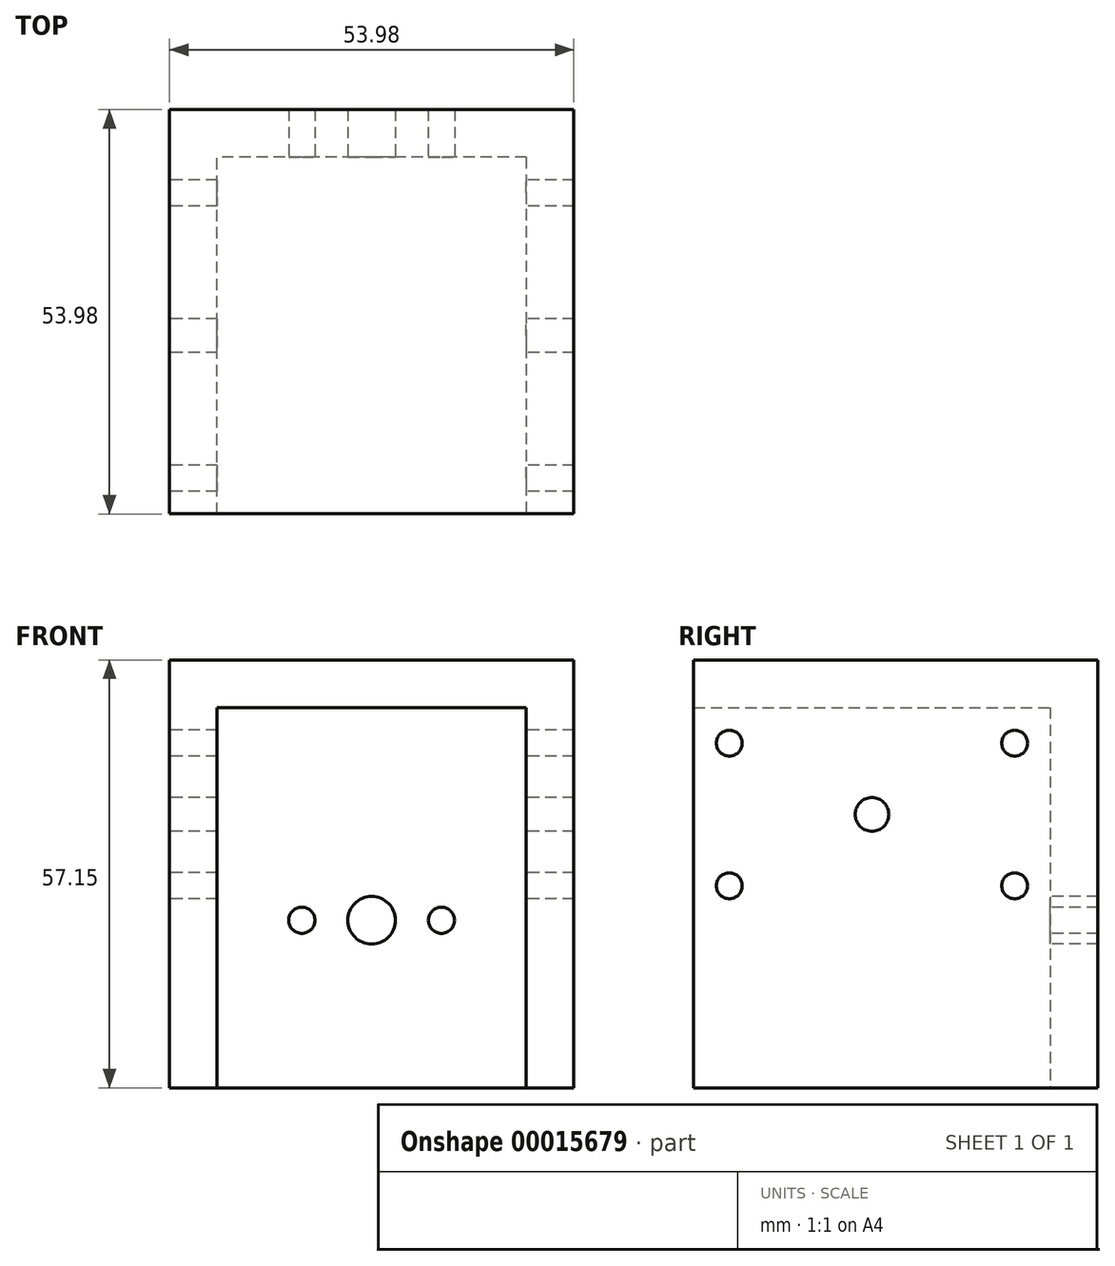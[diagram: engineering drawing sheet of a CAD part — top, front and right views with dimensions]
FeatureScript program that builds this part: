
annotation { "Feature Type Name" : "Feature", "Feature Type Description" : "" }
export const myFeature = defineFeature(function(context is Context, id is Id, definition is map)
    precondition{}
    {
        {
            var Q0;
            Q0=qCreatedBy(makeId("Top.planeOp"),FACE);
            var sketch = newSketch(context, id + "F0", { "sketchPlane" : qUnion([Q0])});
            skLineSegment(sketch, "E0.bottom", {"start": v(0, 0) * mm, "end": v(53.98, 0) * mm});
            skLineSegment(sketch, "E0.left", {"start": v(0, 0) * mm, "end": v(0, -53.98) * mm});
            skLineSegment(sketch, "E1.top", {"start": v(47.62, -6.35) * mm, "end": v(6.35, -6.35) * mm});
            skLineSegment(sketch, "E1.right", {"start": v(6.35, -53.98) * mm, "end": v(6.35, -6.35) * mm});
            skLineSegment(sketch, "E2", {"start": v(0, -53.98) * mm, "end": v(6.35, -53.98) * mm});
            skLineSegment(sketch, "E3", {"start": v(53.98, -53.98) * mm, "end": v(53.98, 0) * mm});
            skLineSegment(sketch, "E4.top", {"start": v(47.63, -53.97) * mm, "end": v(53.98, -53.97) * mm});
            skLineSegment(sketch, "E4.left", {"start": v(47.63, -6.35) * mm, "end": v(47.63, -53.97) * mm});
            skLineSegment(sketch, "E5", {"start": v(26.99, -6.35) * mm, "end": v(26.99, 0) * mm, "construction": true});
            skSolve(sketch);
        }
        {
            var Q0;
            Q0=qSketchRegion(id+"F0",true);
            extrude(context, id + "F1", {"entities" : qUnion([Q0]), "depth" : 50.8 * mm});
        }
        {
            var Q0;
            Q0=makeQuery(id+"F1.opExtrude","SWEPT_FACE",FACE,{"disambiguationData":[OSD([sQuery(id+"F0.wireOp",EDGE,"E0.left")])]});
            var sketch = newSketch(context, id + "F2", { "sketchPlane" : qUnion([Q0])});
            skLineSegment(sketch, "E6.bottom", {"start": v(11.11, 46.04) * mm, "end": v(49.21, 46.04) * mm, "construction": true});
            skLineSegment(sketch, "E6.top", {"start": v(11.11, 26.99) * mm, "end": v(49.21, 26.99) * mm, "construction": true});
            skLineSegment(sketch, "E6.left", {"start": v(49.21, 46.04) * mm, "end": v(49.21, 26.99) * mm, "construction": true});
            skLineSegment(sketch, "E6.right", {"start": v(11.11, 46.04) * mm, "end": v(11.11, 26.99) * mm, "construction": true});
            skPoint(sketch, "E6.middle", {"position": v(30.16, 36.51) * mm});
            skLineSegment(sketch, "E7.bottom", {"start": v(53.98, 46.04) * mm, "end": v(49.21, 46.04) * mm, "construction": true});
            skLineSegment(sketch, "E7.top", {"start": v(53.98, 50.8) * mm, "end": v(49.21, 50.8) * mm, "construction": true});
            skLineSegment(sketch, "E7.left", {"start": v(49.21, 46.04) * mm, "end": v(49.21, 50.8) * mm, "construction": true});
            skLineSegment(sketch, "E7.right", {"start": v(53.98, 46.04) * mm, "end": v(53.98, 50.8) * mm, "construction": true});
            skCircle(sketch, "E8", {"center": v(11.11, 46.04) * mm, "radius": 1.73 * mm});
            skCircle(sketch, "E9", {"center": v(11.11, 26.99) * mm, "radius": 1.73 * mm});
            skCircle(sketch, "E10", {"center": v(49.21, 46.04) * mm, "radius": 1.73 * mm});
            skCircle(sketch, "E11", {"center": v(30.16, 36.51) * mm, "radius": 2.25 * mm});
            skCircle(sketch, "E12", {"center": v(49.21, 26.99) * mm, "radius": 1.73 * mm});
            skSolve(sketch);
        }
        {
            var Q0;
            Q0=qSketchRegion(id+"F2",true);
            var Q1;
            Q1=makeQuery(id+"F1.opExtrude","SWEPT_FACE",FACE,{"disambiguationData":[OSD([sQuery(id+"F0.wireOp",EDGE,"E3")])]});
            extrude(context, id + "F3", {"entities" : qUnion([Q0]), "operationType" : NewBodyOperationType.REMOVE, "endBound" : BoundingType.UP_TO_SURFACE, "oppositeDirection" : true, "endBoundEntityFace" : qUnion([Q1]), "depth" : 25.4 * mm});
        }
        {
            var Q0;
            Q0=makeQuery(id+"F1.opExtrude","CAP_FACE",FACE,{"disambiguationData":[OSD([sQuery(id+"F0.wireOp",EDGE,"E0.bottom"),sQuery(id+"F0.wireOp",EDGE,"E0.left"),sQuery(id+"F0.wireOp",EDGE,"E1.top"),sQuery(id+"F0.wireOp",EDGE,"E1.right"),sQuery(id+"F0.wireOp",EDGE,"E2"),sQuery(id+"F0.wireOp",EDGE,"E3"),sQuery(id+"F0.wireOp",EDGE,"E4.top"),sQuery(id+"F0.wireOp",EDGE,"E4.left")])],"isStart":false});
            var sketch = newSketch(context, id + "F4", { "sketchPlane" : qUnion([Q0])});
            skLineSegment(sketch, "E13.bottom", {"start": v(0, -53.98) * mm, "end": v(53.98, -53.98) * mm});
            skLineSegment(sketch, "E13.top", {"start": v(0, 0) * mm, "end": v(53.98, 0) * mm});
            skLineSegment(sketch, "E13.left", {"start": v(0, -53.98) * mm, "end": v(0, 0) * mm});
            skLineSegment(sketch, "E13.right", {"start": v(53.98, -53.98) * mm, "end": v(53.98, 0) * mm});
            skSolve(sketch);
        }
        {
            var Q0;
            Q0 = qSketchRegion(id + "F4", true);
            extrude(context, id + "F5", {"entities" : qUnion([Q0]), "operationType" : NewBodyOperationType.ADD, "depth" : 6.35 * mm});
        }
        {
            var Q0;
            Q0=makeQuery(id+"F1.opExtrude","SWEPT_FACE",FACE,{"disambiguationData":[OSD([sQuery(id+"F0.wireOp",EDGE,"E1.top")])]});
            var sketch = newSketch(context, id + "F6", { "sketchPlane" : qUnion([Q0])});
            skLineSegment(sketch, "E14", {"start": v(26.99, 0) * mm, "end": v(26.99, 22.38) * mm, "construction": true});
            skLineSegment(sketch, "E15", {"start": v(17.66, 22.38) * mm, "end": v(36.31, 22.38) * mm, "construction": true});
            skCircle(sketch, "E16", {"center": v(26.99, 22.38) * mm, "radius": 3.18 * mm});
            skCircle(sketch, "E17", {"center": v(17.66, 22.38) * mm, "radius": 1.75 * mm});
            skCircle(sketch, "E18", {"center": v(36.31, 22.38) * mm, "radius": 1.75 * mm});
            skSolve(sketch);
        }
        {
            var Q0;
            Q0 = qSketchRegion(id + "F6", true);
            var Q1;
            Q1=makeQuery(id+"F5.boolean.opBoolean","MERGE",FACE,{"derivedFrom":[makeQuery(id+"F1.opExtrude","SWEPT_FACE",FACE,{"disambiguationData":[OSD([sQuery(id+"F0.wireOp",EDGE,"E0.bottom")])]}),makeQuery(id+"F5.opExtrude","SWEPT_FACE",FACE,{"disambiguationData":[OSD([sQuery(id+"F4.wireOp",EDGE,"E13.top")])]})]});
            extrude(context, id + "F7", {"entities" : qUnion([Q0]), "operationType" : NewBodyOperationType.REMOVE, "endBound" : BoundingType.UP_TO_SURFACE, "oppositeDirection" : true, "endBoundEntityFace" : qUnion([Q1]), "depth" : 25.4 * mm});
        }
    });
